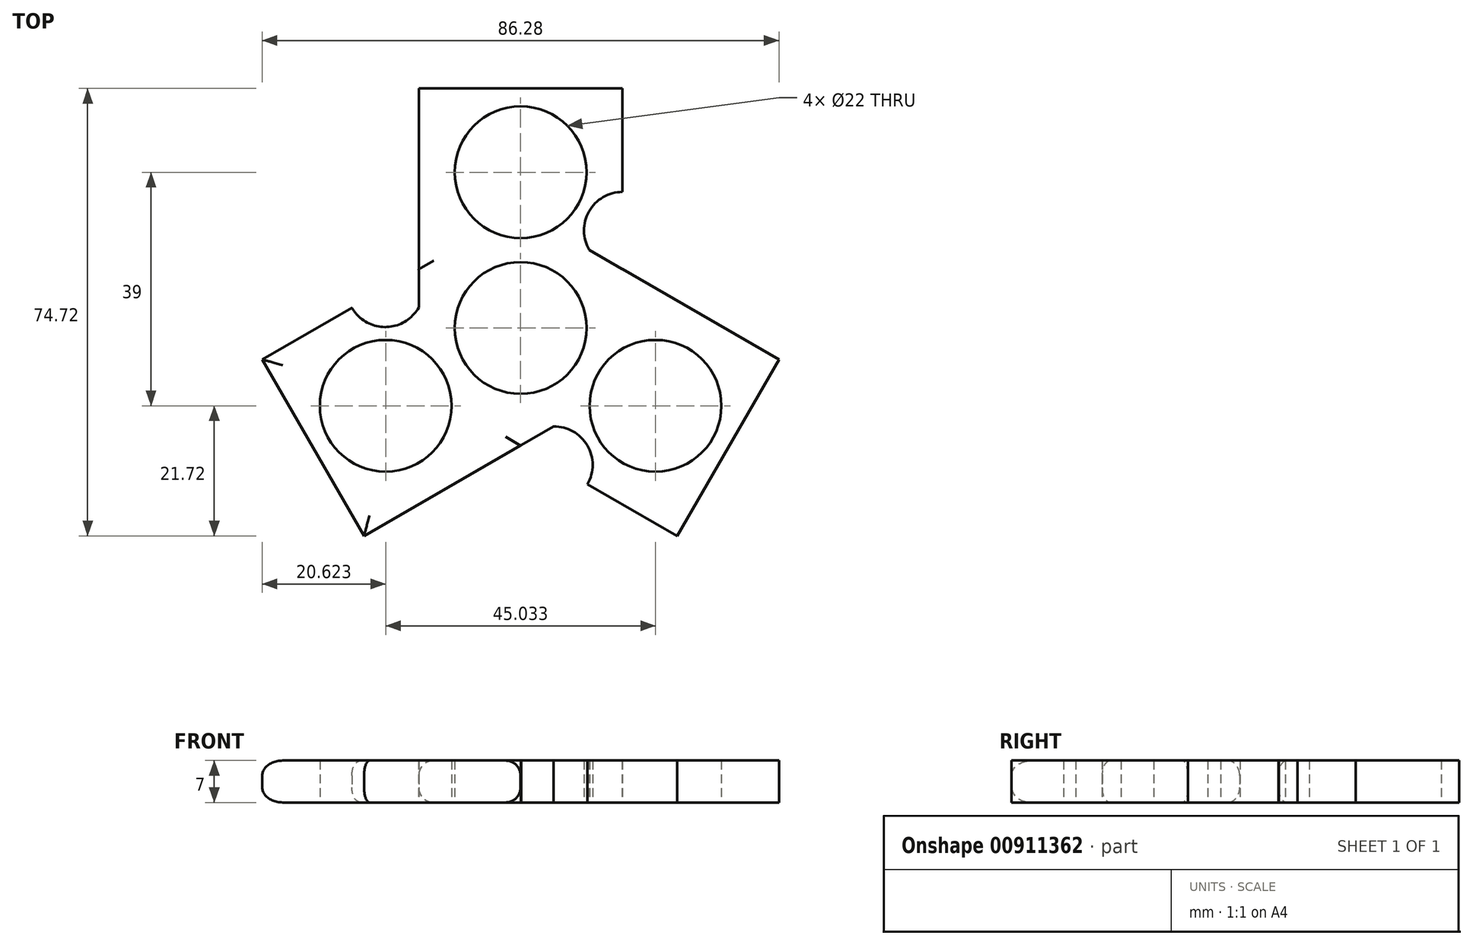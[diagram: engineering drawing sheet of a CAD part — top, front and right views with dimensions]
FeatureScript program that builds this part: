
annotation { "Feature Type Name" : "Feature", "Feature Type Description" : "" }
export const myFeature = defineFeature(function(context is Context, id is Id, definition is map)
    precondition{}
    {
        {
            var Q0;
            Q0=qCreatedBy(makeId("Top.planeOp"),FACE);
            var sketch = newSketch(context, id + "F0", { "sketchPlane" : qUnion([Q0])});
            skCircle(sketch, "E0", {"center": v(0, 0) * mm, "radius": 11 * mm});
            skLineSegment(sketch, "E1.bottom", {"start": v(0, 0) * mm, "end": v(17, 0) * mm});
            skLineSegment(sketch, "E1.top", {"start": v(0, 40) * mm, "end": v(17, 40) * mm});
            skLineSegment(sketch, "E1.left", {"start": v(0, 0) * mm, "end": v(0, 40) * mm});
            skLineSegment(sketch, "E1.right", {"start": v(17, 0) * mm, "end": v(17, 40) * mm});
            skLineSegment(sketch, "E2.bottom", {"start": v(0, 0) * mm, "end": v(-17, 0) * mm});
            skLineSegment(sketch, "E2.top", {"start": v(0, 40) * mm, "end": v(-17, 40) * mm});
            skLineSegment(sketch, "E2.right", {"start": v(-17, 0) * mm, "end": v(-17, 40) * mm});
            skLineSegment(sketch, "E3", {"start": v(0, 40) * mm, "end": v(0, 26) * mm});
            skCircle(sketch, "E4", {"center": v(0, 26) * mm, "radius": 11 * mm});
            skCircle(sketch, "E5", {"center": v(17, 16.29) * mm, "radius": 6.42 * mm});
            skSolve(sketch);
        }
        {
            var Q0;
            {var subQ0=sQuery(id+"F0.wireOp",EDGE,"E2.top");Q0=makeQuery(id+"F0.imprint","IMPRINT",FACE,{"disambiguationData":[TD([[makeQuery(id+"F0.imprint","IMPRINT",EDGE,{"derivedFrom":subQ0}),1.0]])]});}
            var Q1;
            {var subQ9=sQuery(id+"F0.wireOp",EDGE,"E1.top");Q1=makeQuery(id+"F0.imprint","IMPRINT",FACE,{"disambiguationData":[TD([[makeQuery(id+"F0.imprint","IMPRINT",EDGE,{"derivedFrom":subQ9}),-1.0]])]});}
            extrude(context, id + "F1", {"entities" : qUnion([Q0, Q1]), "depth" : 7 * mm, "offsetDistance" : 25 * mm});
        }
        {
            var Q0;
            Q0=qCreatedBy(makeId("Front.planeOp"),FACE);
            var sketch = newSketch(context, id + "F2", { "sketchPlane" : qUnion([Q0])});
            skLineSegment(sketch, "E6", {"start": v(0, 0) * mm, "end": v(0, 49.55) * mm});
            skSolve(sketch);
        }
        {
            var Q0;
            Q0=makeQuery(id+"F1.opExtrude","SWEPT_BODY",BODY,{"disambiguationData":[OSD([sQuery(id+"F0.wireOp",EDGE,"E0"),sQuery(id+"F0.wireOp",EDGE,"E1.bottom"),sQuery(id+"F0.wireOp",EDGE,"E1.top"),sQuery(id+"F0.wireOp",EDGE,"E1.right"),sQuery(id+"F0.wireOp",EDGE,"E2.bottom"),sQuery(id+"F0.wireOp",EDGE,"E2.top"),sQuery(id+"F0.wireOp",EDGE,"E2.right"),sQuery(id+"F0.wireOp",EDGE,"E4")])]});
            var Q1;
            Q1=sQuery(id+"F2.wireOp",EDGE,"E6");
            transform(context, id + "F3", {"entities" : qUnion([Q0]), "transformType" : TransformType.ROTATION, "transformAxis" : qUnion([Q1]), "angle" : 240 * degree, "makeCopy" : true});
        }
        {
            var Q0;
            Q0=makeQuery(id+"F1.opExtrude","SWEPT_BODY",BODY,{"disambiguationData":[OSD([sQuery(id+"F0.wireOp",EDGE,"E0"),sQuery(id+"F0.wireOp",EDGE,"E1.bottom"),sQuery(id+"F0.wireOp",EDGE,"E1.top"),sQuery(id+"F0.wireOp",EDGE,"E1.right"),sQuery(id+"F0.wireOp",EDGE,"E2.bottom"),sQuery(id+"F0.wireOp",EDGE,"E2.top"),sQuery(id+"F0.wireOp",EDGE,"E2.right"),sQuery(id+"F0.wireOp",EDGE,"E4")])]});
            var Q1;
            Q1=sQuery(id+"F2.wireOp",EDGE,"E6");
            transform(context, id + "F4", {"entities" : qUnion([Q0]), "transformType" : TransformType.ROTATION, "transformAxis" : qUnion([Q1]), "angle" : 120 * degree, "makeCopy" : true});
        }
        {
            var Q0;
            Q0=makeQuery(id+"F1.opExtrude","SWEPT_BODY",BODY,{"disambiguationData":[OSD([sQuery(id+"F0.wireOp",EDGE,"E0"),sQuery(id+"F0.wireOp",EDGE,"E1.bottom"),sQuery(id+"F0.wireOp",EDGE,"E1.top"),sQuery(id+"F0.wireOp",EDGE,"E1.right"),sQuery(id+"F0.wireOp",EDGE,"E2.bottom"),sQuery(id+"F0.wireOp",EDGE,"E2.top"),sQuery(id+"F0.wireOp",EDGE,"E2.right"),sQuery(id+"F0.wireOp",EDGE,"E4")])]});
            var Q1;
            Q1=makeQuery(id+"F3.opPattern","COPY",BODY,{"derivedFrom":makeQuery(id+"F1.opExtrude","SWEPT_BODY",BODY,{"disambiguationData":[OSD([sQuery(id+"F0.wireOp",EDGE,"E0"),sQuery(id+"F0.wireOp",EDGE,"E1.bottom"),sQuery(id+"F0.wireOp",EDGE,"E1.top"),sQuery(id+"F0.wireOp",EDGE,"E1.right"),sQuery(id+"F0.wireOp",EDGE,"E2.bottom"),sQuery(id+"F0.wireOp",EDGE,"E2.top"),sQuery(id+"F0.wireOp",EDGE,"E2.right"),sQuery(id+"F0.wireOp",EDGE,"E4")])]}),"instanceName":"1"});
            var Q2;
            Q2=makeQuery(id+"F4.opPattern","COPY",BODY,{"derivedFrom":makeQuery(id+"F1.opExtrude","SWEPT_BODY",BODY,{"disambiguationData":[OSD([sQuery(id+"F0.wireOp",EDGE,"E0"),sQuery(id+"F0.wireOp",EDGE,"E1.bottom"),sQuery(id+"F0.wireOp",EDGE,"E1.top"),sQuery(id+"F0.wireOp",EDGE,"E1.right"),sQuery(id+"F0.wireOp",EDGE,"E2.bottom"),sQuery(id+"F0.wireOp",EDGE,"E2.top"),sQuery(id+"F0.wireOp",EDGE,"E2.right"),sQuery(id+"F0.wireOp",EDGE,"E4")])]}),"instanceName":"1"});
            booleanBodies(context, id + "F5", {"operationType" : BooleanOperationType.UNION, "tools" : qUnion([Q0, Q1, Q2])});
        }
        {
            var Q0;
            {var subQ0=sQuery(id+"F0.wireOp",EDGE,"E2.right");var subQ2=sQuery(id+"F0.wireOp",EDGE,"E2.top");var subQ4=sQuery(id+"F0.wireOp",EDGE,"E1.top");Q0=makeQuery(id+"F5.opBoolean","SPLIT",EDGE,{"disambiguationData":[TD([makeQuery(id+"F1.opExtrude","SWEPT_FACE",FACE,{"disambiguationData":[OSD([subQ4,subQ2])]})])],"derivedFrom":makeQuery(id+"F1.opExtrude","CAP_EDGE",EDGE,{"disambiguationData":[OSD([subQ0])],"isStart":false})});}
            var Q1;
            {var subQ1=sQuery(id+"F0.wireOp",EDGE,"E2.right");var subQ2=sQuery(id+"F0.wireOp",EDGE,"E2.top");var subQ4=sQuery(id+"F0.wireOp",EDGE,"E1.top");Q1=makeQuery(id+"F5.opBoolean","SPLIT",EDGE,{"disambiguationData":[TD([makeQuery(id+"F1.opExtrude","SWEPT_FACE",FACE,{"disambiguationData":[OSD([subQ4,subQ2])]})])],"derivedFrom":makeQuery(id+"F1.opExtrude","CAP_EDGE",EDGE,{"disambiguationData":[OSD([subQ1])],"isStart":true})});}
            var Q2;
            {var subQ0=sQuery(id+"F0.wireOp",EDGE,"E1.right");Q2=makeQuery(id+"F4.opPattern","COPY",EDGE,{"derivedFrom":makeQuery(id+"F1.opExtrude","CAP_EDGE",EDGE,{"disambiguationData":[OSD([subQ0]),TDD([makeQuery(id+"F0.imprint","IMPRINT",EDGE,{"disambiguationData":[TD([[makeQuery(id+"F0.imprint","INTERSECT",VERTEX,{"derivedFrom":[sQuery(id+"F0.wireOp",EDGE,"E1.top"),subQ0]}),1.0]])],"derivedFrom":subQ0})])],"isStart":false}),"instanceName":"1"});}
            var Q3;
            {var subQ0=sQuery(id+"F0.wireOp",EDGE,"E1.right");Q3=makeQuery(id+"F4.opPattern","COPY",EDGE,{"derivedFrom":makeQuery(id+"F1.opExtrude","CAP_EDGE",EDGE,{"disambiguationData":[OSD([subQ0]),TDD([makeQuery(id+"F0.imprint","IMPRINT",EDGE,{"disambiguationData":[TD([[makeQuery(id+"F0.imprint","INTERSECT",VERTEX,{"derivedFrom":[sQuery(id+"F0.wireOp",EDGE,"E1.top"),subQ0]}),1.0]])],"derivedFrom":subQ0})])],"isStart":true}),"instanceName":"1"});}
            var Q4;
            {var subQ1=sQuery(id+"F0.wireOp",EDGE,"E2.right");var subQ2=sQuery(id+"F0.wireOp",EDGE,"E2.top");var subQ4=sQuery(id+"F0.wireOp",EDGE,"E1.top");Q4=makeQuery(id+"F5.opBoolean","SPLIT",EDGE,{"disambiguationData":[TD([makeQuery(id+"F4.opPattern","COPY",FACE,{"derivedFrom":makeQuery(id+"F1.opExtrude","SWEPT_FACE",FACE,{"disambiguationData":[OSD([subQ4,subQ2])]}),"instanceName":"1"})])],"derivedFrom":makeQuery(id+"F4.opPattern","COPY",EDGE,{"derivedFrom":makeQuery(id+"F1.opExtrude","CAP_EDGE",EDGE,{"disambiguationData":[OSD([subQ1])],"isStart":false}),"instanceName":"1"})});}
            var Q5;
            {var subQ1=sQuery(id+"F0.wireOp",EDGE,"E2.right");var subQ2=sQuery(id+"F0.wireOp",EDGE,"E2.top");var subQ4=sQuery(id+"F0.wireOp",EDGE,"E1.top");Q5=makeQuery(id+"F5.opBoolean","SPLIT",EDGE,{"disambiguationData":[TD([makeQuery(id+"F4.opPattern","COPY",FACE,{"derivedFrom":makeQuery(id+"F1.opExtrude","SWEPT_FACE",FACE,{"disambiguationData":[OSD([subQ4,subQ2])]}),"instanceName":"1"})])],"derivedFrom":makeQuery(id+"F4.opPattern","COPY",EDGE,{"derivedFrom":makeQuery(id+"F1.opExtrude","CAP_EDGE",EDGE,{"disambiguationData":[OSD([subQ1])],"isStart":true}),"instanceName":"1"})});}
            var Q6;
            Q6=makeQuery(id+"F4.opPattern","COPY",EDGE,{"derivedFrom":makeQuery(id+"F1.opExtrude","CAP_EDGE",EDGE,{"disambiguationData":[OSD([sQuery(id+"F0.wireOp",EDGE,"E1.top"),sQuery(id+"F0.wireOp",EDGE,"E2.top")])],"isStart":false}),"instanceName":"1"});
            var Q7;
            Q7=makeQuery(id+"F4.opPattern","COPY",EDGE,{"derivedFrom":makeQuery(id+"F1.opExtrude","CAP_EDGE",EDGE,{"disambiguationData":[OSD([sQuery(id+"F0.wireOp",EDGE,"E1.top"),sQuery(id+"F0.wireOp",EDGE,"E2.top")])],"isStart":true}),"instanceName":"1"});
            fillet(context, id + "F6", {"entities" : qUnion([Q0, Q1, Q2, Q3, Q4, Q5, Q6, Q7]), "radius" : 2.5 * mm, "tangentPropagation" : true, "allowEdgeOverflow" : false});
        }
    });
